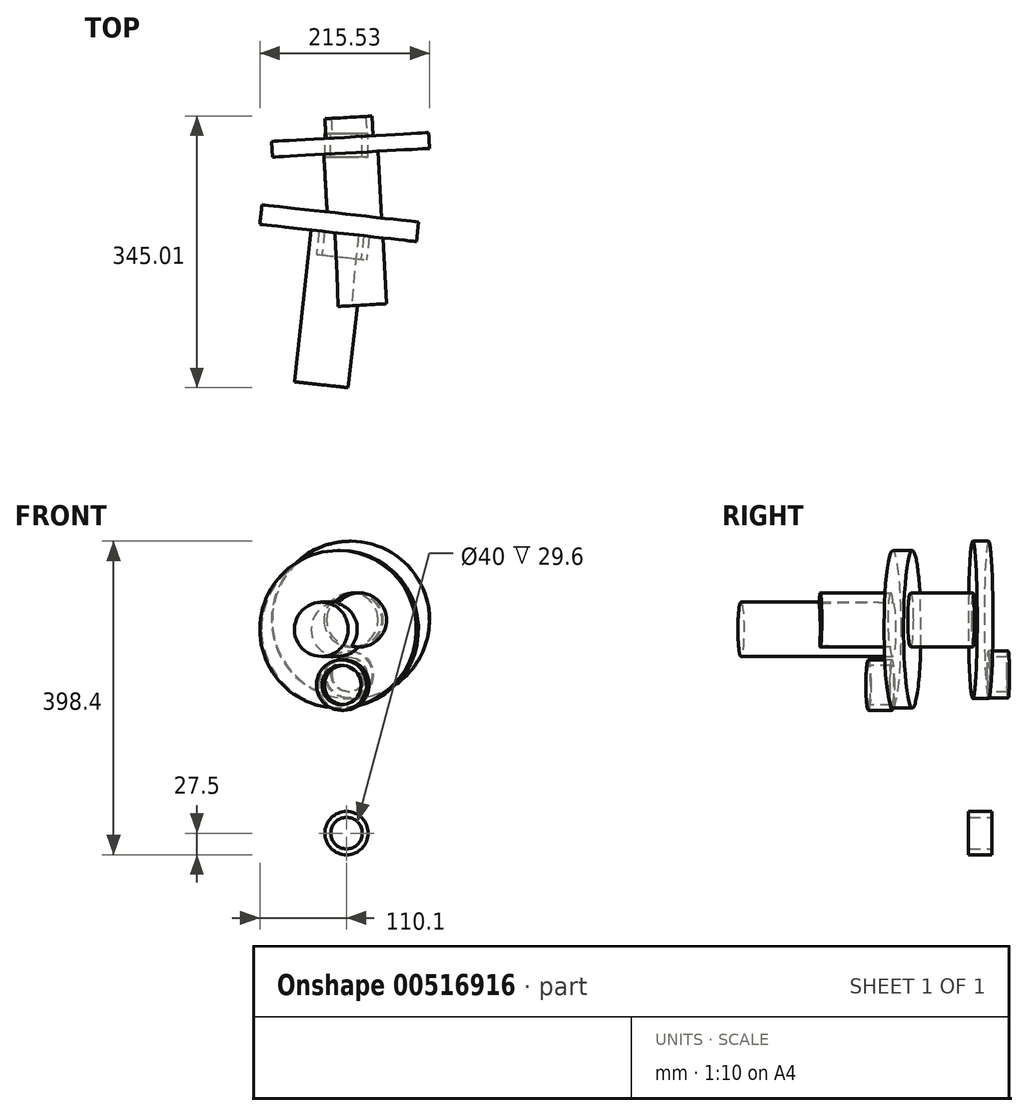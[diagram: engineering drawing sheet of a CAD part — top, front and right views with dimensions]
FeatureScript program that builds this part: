
annotation { "Feature Type Name" : "Feature", "Feature Type Description" : "" }
export const myFeature = defineFeature(function(context is Context, id is Id, definition is map)
    precondition{}
    {
        {
            var Q0;
            Q0=qCreatedBy(makeId("Front.planeOp"),FACE);
            var sketch = newSketch(context, id + "F0", { "sketchPlane" : qUnion([Q0])});
            skLineSegment(sketch, "E0", {"start": v(0, 498.69) * mm, "end": v(0, -551.31) * mm, "construction": true});
            skLineSegment(sketch, "E1", {"start": v(659.07, 0) * mm, "end": v(-656.56, 0) * mm, "construction": true});
            skSolve(sketch);
        }
        {
            var Q0;
            Q0=qCreatedBy(makeId("Front.planeOp"),FACE);
            cPlane(context, id + "F1", {"entities" : qUnion([Q0]), "cplaneType" : CPlaneType.OFFSET, "offset" : 36.2 * mm, "oppositeDirection" : true, "width" : 150 * mm, "height" : 150 * mm});
        }
        {
            var Q0;
            Q0=qCreatedBy(id+"F1.planeOp",FACE);
            var sketch = newSketch(context, id + "F2", { "sketchPlane" : qUnion([Q0])});
            skCircle(sketch, "E2", {"center": v(49.2, -100.9) * mm, "radius": 27.5 * mm});
            skCircle(sketch, "E3", {"center": v(49.2, -100.9) * mm, "radius": 20 * mm});
            skSolve(sketch);
        }
        {
            var Q0;
            Q0 = qSketchRegion(id + "F2", true);
            extrude(context, id + "F3", {"entities" : qUnion([Q0]), "depth" : 14.8 * mm, "offsetDistance" : 25 * mm, "hasSecondDirection" : true, "secondDirectionOppositeDirection" : true, "secondDirectionDepth" : 14.8 * mm});
        }
        {
            var Q0;
            Q0=qCreatedBy(makeId("Front.planeOp"),FACE);
            cPlane(context, id + "F4", {"entities" : qUnion([Q0]), "cplaneType" : CPlaneType.OFFSET, "offset" : 59.2 * mm, "oppositeDirection" : true, "width" : 150 * mm, "height" : 150 * mm});
        }
        {
            var Q0;
            Q0=qCreatedBy(id+"F4.planeOp",FACE);
            var sketch = newSketch(context, id + "F5", { "sketchPlane" : qUnion([Q0])});
            skLineSegment(sketch, "E4", {"start": v(52.4, 141.34) * mm, "end": v(52.4, 3.72) * mm, "construction": true});
            skLineSegment(sketch, "E5", {"start": v(22.34, 100.7) * mm, "end": v(97.97, 100.7) * mm, "construction": true});
            skSolve(sketch);
        }
        {
            var Q0;
            Q0=qCreatedBy(id+"F4.planeOp",FACE);
            var Q1;
            Q1=sQuery(id+"F5.wireOp",EDGE,"E4");
            cPlane(context, id + "F6", {"entities" : qUnion([Q0, Q1]), "cplaneType" : CPlaneType.LINE_ANGLE, "offset" : 25 * mm, "angle" : 3.2 * degree, "oppositeDirection" : true, "width" : 150 * mm, "height" : 150 * mm});
        }
        {
            var Q0;
            Q0=qCreatedBy(id+"F6.planeOp",FACE);
            var sketch = newSketch(context, id + "F7", { "sketchPlane" : qUnion([Q0])});
            skCircle(sketch, "E6", {"center": v(-55.62, 100.7) * mm, "radius": 30 * mm});
            skCircle(sketch, "E7", {"center": v(-55.62, 100.7) * mm, "radius": 22 * mm});
            skSolve(sketch);
        }
        {
            var Q0;
            Q0 = qSketchRegion(id + "F7", true);
            extrude(context, id + "F8", {"entities" : qUnion([Q0]), "depth" : 12.5 * mm, "offsetDistance" : 25 * mm, "hasSecondDirection" : true, "secondDirectionOppositeDirection" : true, "secondDirectionDepth" : 12.5 * mm});
        }
        {
            var Q0;
            Q0=qCreatedBy(makeId("Front.planeOp"),FACE);
            cPlane(context, id + "F9", {"entities" : qUnion([Q0]), "cplaneType" : CPlaneType.OFFSET, "offset" : 90.8 * mm, "width" : 150 * mm, "height" : 150 * mm});
        }
        {
            var Q0;
            Q0=qCreatedBy(id+"F9.planeOp",FACE);
            var sketch = newSketch(context, id + "F10", { "sketchPlane" : qUnion([Q0])});
            skLineSegment(sketch, "E8", {"start": v(44.5, 208.95) * mm, "end": v(44.5, -169.2) * mm, "construction": true});
            skLineSegment(sketch, "E9", {"start": v(223.25, 87.3) * mm, "end": v(-34.44, 87.3) * mm, "construction": true});
            skSolve(sketch);
        }
        {
            var Q0;
            Q0=qCreatedBy(id+"F9.planeOp",FACE);
            var Q1;
            Q1=sQuery(id+"F10.wireOp",EDGE,"E8");
            cPlane(context, id + "F11", {"entities" : qUnion([Q0, Q1]), "cplaneType" : CPlaneType.LINE_ANGLE, "offset" : 25 * mm, "angle" : 6.3 * degree, "width" : 150 * mm, "height" : 150 * mm});
        }
        {
            var Q0;
            Q0=qCreatedBy(id+"F11.planeOp",FACE);
            var sketch = newSketch(context, id + "F12", { "sketchPlane" : qUnion([Q0])});
            skCircle(sketch, "E10", {"center": v(-54.2, 87.3) * mm, "radius": 32 * mm});
            skCircle(sketch, "E11", {"center": v(-54.2, 87.3) * mm, "radius": 25 * mm});
            skSolve(sketch);
        }
        {
            var Q0;
            Q0 = qSketchRegion(id + "F12", true);
            extrude(context, id + "F13", {"entities" : qUnion([Q0]), "depth" : 15 * mm, "offsetDistance" : 25 * mm, "hasSecondDirection" : true, "secondDirectionOppositeDirection" : true, "secondDirectionDepth" : 15 * mm});
        }
        {
            var Q0;
            Q0=makeQuery(id+"F8.opExtrude","CAP_FACE",FACE,{"disambiguationData":[OSD([sQuery(id+"F7.wireOp",EDGE,"E6"),sQuery(id+"F7.wireOp",EDGE,"E7")])],"isStart":true});
            var sketch = newSketch(context, id + "F14", { "sketchPlane" : qUnion([Q0])});
            skCircle(sketch, "E12", {"center": v(56.2, 170) * mm, "radius": 100 * mm});
            skSolve(sketch);
        }
        {
            var Q0;
            Q0 = qSketchRegion(id + "F14", true);
            extrude(context, id + "F15", {"entities" : qUnion([Q0]), "depth" : 20 * mm, "offsetDistance" : 25 * mm});
        }
        {
            var Q0;
            Q0=makeQuery(id+"F15.opExtrude","CAP_FACE",FACE,{"disambiguationData":[OSD([sQuery(id+"F14.wireOp",EDGE,"E12")])],"isStart":false});
            var sketch = newSketch(context, id + "F16", { "sketchPlane" : qUnion([Q0])});
            skCircle(sketch, "E13", {"center": v(56.2, 170) * mm, "radius": 34.4 * mm});
            skSolve(sketch);
        }
        {
            var Q0;
            Q0 = qSketchRegion(id + "F16", true);
            extrude(context, id + "F17", {"entities" : qUnion([Q0]), "operationType" : NewBodyOperationType.ADD, "depth" : 194 * mm, "offsetDistance" : 25 * mm});
        }
        {
            var Q0;
            Q0=makeQuery(id+"F13.opExtrude","CAP_FACE",FACE,{"disambiguationData":[OSD([sQuery(id+"F12.wireOp",EDGE,"E10"),sQuery(id+"F12.wireOp",EDGE,"E11")])],"isStart":false});
            var sketch = newSketch(context, id + "F18", { "sketchPlane" : qUnion([Q0])});
            skCircle(sketch, "E14", {"center": v(-46.5, 158.1) * mm, "radius": 100 * mm});
            skSolve(sketch);
        }
        {
            var Q0;
            Q0 = qSketchRegion(id + "F18", true);
            extrude(context, id + "F19", {"entities" : qUnion([Q0]), "depth" : 25 * mm, "offsetDistance" : 25 * mm});
        }
        {
            var Q0;
            Q0=makeQuery(id+"F19.opExtrude","CAP_FACE",FACE,{"disambiguationData":[OSD([sQuery(id+"F18.wireOp",EDGE,"E14")])],"isStart":true});
            var sketch = newSketch(context, id + "F20", { "sketchPlane" : qUnion([Q0])});
            skCircle(sketch, "E15", {"center": v(46.5, 158.1) * mm, "radius": 34.4 * mm});
            skSolve(sketch);
        }
        {
            var Q0;
            Q0 = qSketchRegion(id + "F20", true);
            extrude(context, id + "F21", {"entities" : qUnion([Q0]), "operationType" : NewBodyOperationType.ADD, "depth" : 194 * mm, "offsetDistance" : 25 * mm});
        }
    });
